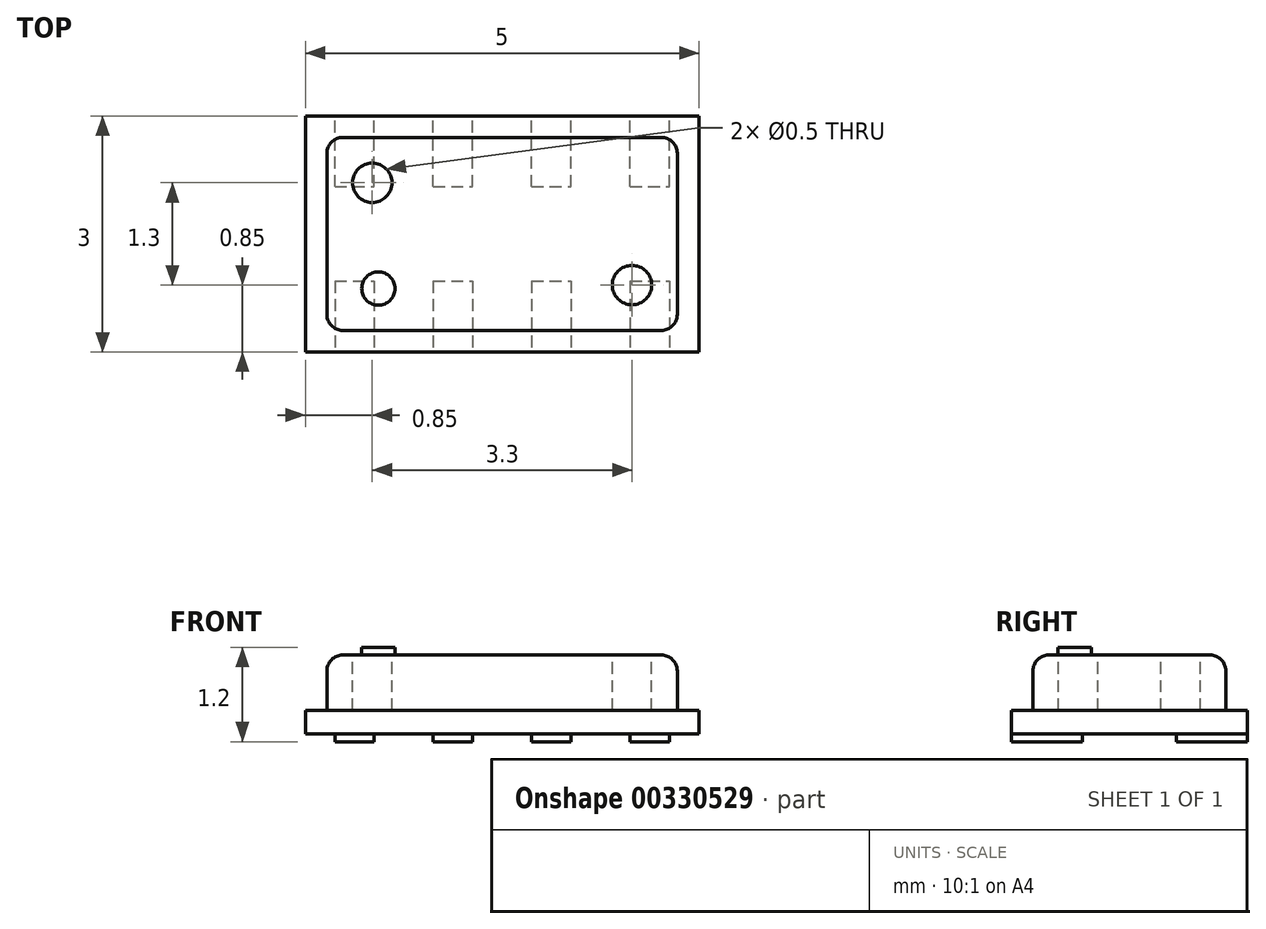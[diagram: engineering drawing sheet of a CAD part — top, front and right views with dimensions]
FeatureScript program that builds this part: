
annotation { "Feature Type Name" : "Feature", "Feature Type Description" : "" }
export const myFeature = defineFeature(function(context is Context, id is Id, definition is map)
    precondition{}
    {
        {
            var Q0;
            Q0=qCreatedBy(makeId("Top.planeOp"),FACE);
            var sketch = newSketch(context, id + "F0", { "sketchPlane" : qUnion([Q0])});
            skLineSegment(sketch, "E0.bottom", {"start": v(2.5, -1.5) * mm, "end": v(-2.5, -1.5) * mm});
            skLineSegment(sketch, "E0.top", {"start": v(2.5, 1.5) * mm, "end": v(-2.5, 1.5) * mm});
            skLineSegment(sketch, "E0.left", {"start": v(2.5, -1.5) * mm, "end": v(2.5, 1.5) * mm});
            skLineSegment(sketch, "E0.right", {"start": v(-2.5, -1.5) * mm, "end": v(-2.5, 1.5) * mm});
            skPoint(sketch, "E0.middle", {"position": v(0, 0) * mm});
            skSolve(sketch);
        }
        {
            var Q0;
            Q0 = qSketchRegion(id + "F0", true);
            extrude(context, id + "F1", {"entities" : qUnion([Q0]), "depth" : .3 * mm, "offsetDistance" : 25 * mm});
        }
        {
            var Q0;
            Q0=makeQuery(id+"F1.opExtrude","CAP_FACE",FACE,{"disambiguationData":[OSD([sQuery(id+"F0.wireOp",EDGE,"E0.bottom"),sQuery(id+"F0.wireOp",EDGE,"E0.top"),sQuery(id+"F0.wireOp",EDGE,"E0.left"),sQuery(id+"F0.wireOp",EDGE,"E0.right")])],"isStart":false});
            var sketch = newSketch(context, id + "F2", { "sketchPlane" : qUnion([Q0])});
            skLineSegment(sketch, "E1.bottom", {"start": v(2.23, -1.23) * mm, "end": v(-2.23, -1.23) * mm});
            skLineSegment(sketch, "E1.top", {"start": v(2.23, 1.23) * mm, "end": v(-2.23, 1.23) * mm});
            skLineSegment(sketch, "E1.left", {"start": v(2.23, -1.23) * mm, "end": v(2.23, 1.23) * mm});
            skLineSegment(sketch, "E1.right", {"start": v(-2.23, -1.23) * mm, "end": v(-2.23, 1.23) * mm});
            skPoint(sketch, "E1.middle", {"position": v(0, 0) * mm});
            skSolve(sketch);
        }
        {
            var Q0;
            Q0 = qSketchRegion(id + "F2", true);
            extrude(context, id + "F3", {"entities" : qUnion([Q0]), "depth" : .7 * mm, "offsetDistance" : 25 * mm});
        }
        {
            var Q0;
            Q0=makeQuery(id+"F3.opExtrude","CAP_EDGE",EDGE,{"disambiguationData":[OSD([sQuery(id+"F2.wireOp",EDGE,"E1.bottom")])],"isStart":false});
            var Q1;
            Q1=makeQuery(id+"F3.opExtrude","CAP_EDGE",EDGE,{"disambiguationData":[OSD([sQuery(id+"F2.wireOp",EDGE,"E1.left")])],"isStart":false});
            var Q2;
            Q2=makeQuery(id+"F3.opExtrude","CAP_EDGE",EDGE,{"disambiguationData":[OSD([sQuery(id+"F2.wireOp",EDGE,"E1.top")])],"isStart":false});
            var Q3;
            Q3=makeQuery(id+"F3.opExtrude","CAP_EDGE",EDGE,{"disambiguationData":[OSD([sQuery(id+"F2.wireOp",EDGE,"E1.right")])],"isStart":false});
            var Q4;
            Q4=makeQuery(id+"F3.opExtrude","SWEPT_EDGE",EDGE,{"disambiguationData":[OSD([sQuery(id+"F2.wireOp",EDGE,"E1.top"),sQuery(id+"F2.wireOp",EDGE,"E1.right")])]});
            var Q5;
            Q5=makeQuery(id+"F3.opExtrude","SWEPT_EDGE",EDGE,{"disambiguationData":[OSD([sQuery(id+"F2.wireOp",EDGE,"E1.bottom"),sQuery(id+"F2.wireOp",EDGE,"E1.right")])]});
            var Q6;
            Q6=makeQuery(id+"F3.opExtrude","SWEPT_EDGE",EDGE,{"disambiguationData":[OSD([sQuery(id+"F2.wireOp",EDGE,"E1.bottom"),sQuery(id+"F2.wireOp",EDGE,"E1.left")])]});
            var Q7;
            Q7=makeQuery(id+"F3.opExtrude","SWEPT_EDGE",EDGE,{"disambiguationData":[OSD([sQuery(id+"F2.wireOp",EDGE,"E1.top"),sQuery(id+"F2.wireOp",EDGE,"E1.left")])]});
            fillet(context, id + "F4", {"entities" : qUnion([Q0, Q1, Q2, Q3, Q4, Q5, Q6, Q7]), "radius" : .2 * mm, "tangentPropagation" : true, "allowEdgeOverflow" : false});
        }
        {
            var Q0;
            Q0=makeQuery(id+"F3.opExtrude","CAP_FACE",FACE,{"disambiguationData":[OSD([sQuery(id+"F2.wireOp",EDGE,"E1.bottom"),sQuery(id+"F2.wireOp",EDGE,"E1.top"),sQuery(id+"F2.wireOp",EDGE,"E1.left"),sQuery(id+"F2.wireOp",EDGE,"E1.right")])],"isStart":false});
            var sketch = newSketch(context, id + "F5", { "sketchPlane" : qUnion([Q0])});
            skCircle(sketch, "E2", {"center": v(1.65, -0.65) * mm, "radius": 0.25 * mm});
            skCircle(sketch, "E3", {"center": v(-1.65, 0.65) * mm, "radius": 0.25 * mm});
            skLineSegment(sketch, "E4", {"start": v(2.5, 0) * mm, "end": v(-2.43, 0) * mm, "construction": true});
            skLineSegment(sketch, "E5", {"start": v(0, 1.03) * mm, "end": v(0, -1.12) * mm, "construction": true});
            skPoint(sketch, "E5.endSnap0", {"position": v(0, -1.03) * mm});
            skSolve(sketch);
        }
        {
            var Q0;
            Q0 = qSketchRegion(id + "F5", true);
            extrude(context, id + "F6", {"entities" : qUnion([Q0]), "operationType" : NewBodyOperationType.REMOVE, "endBound" : BoundingType.UP_TO_NEXT, "oppositeDirection" : true, "depth" : 4 * mm, "offsetDistance" : 25 * mm});
        }
        {
            var Q0;
            Q0=makeQuery(id+"F1.opExtrude","CAP_FACE",FACE,{"disambiguationData":[OSD([sQuery(id+"F0.wireOp",EDGE,"E0.bottom"),sQuery(id+"F0.wireOp",EDGE,"E0.top"),sQuery(id+"F0.wireOp",EDGE,"E0.left"),sQuery(id+"F0.wireOp",EDGE,"E0.right")])],"isStart":true});
            var sketch = newSketch(context, id + "F7", { "sketchPlane" : qUnion([Q0])});
            skLineSegment(sketch, "E6", {"start": v(2.5, 0) * mm, "end": v(-2.5, 0) * mm, "construction": true});
            skLineSegment(sketch, "E7.bottom", {"start": v(1.63, 0.6) * mm, "end": v(2.12, 0.6) * mm});
            skLineSegment(sketch, "E7.top", {"start": v(1.63, 1.5) * mm, "end": v(2.12, 1.5) * mm});
            skLineSegment(sketch, "E7.left", {"start": v(1.63, 0.6) * mm, "end": v(1.63, 1.5) * mm});
            skLineSegment(sketch, "E7.right", {"start": v(2.12, 0.6) * mm, "end": v(2.12, 1.5) * mm});
            skPoint(sketch, "E7.middle", {"position": v(1.88, 1.05) * mm});
            skLineSegment(sketch, "E8", {"start": v(0, 1.5) * mm, "end": v(0, -0.09) * mm, "construction": true});
            skPoint(sketch, "E8.endSnap0", {"position": v(0, 1.5) * mm});
            skPoint(sketch, "E9.1.0.0", {"position": v(0.62, 1.05) * mm});
            skLineSegment(sketch, "E9.1.0.1", {"start": v(0.38, 0.6) * mm, "end": v(0.88, 0.6) * mm});
            skLineSegment(sketch, "E9.1.0.2", {"start": v(0.38, 1.5) * mm, "end": v(0.88, 1.5) * mm});
            skLineSegment(sketch, "E9.1.0.3", {"start": v(0.88, 0.6) * mm, "end": v(0.88, 1.5) * mm});
            skLineSegment(sketch, "E9.1.0.4", {"start": v(0.38, 0.6) * mm, "end": v(0.38, 1.5) * mm});
            skPoint(sketch, "E9.2.0.0", {"position": v(-0.63, 1.05) * mm});
            skLineSegment(sketch, "E9.2.0.1", {"start": v(-0.87, 0.6) * mm, "end": v(-0.37, 0.6) * mm});
            skLineSegment(sketch, "E9.2.0.2", {"start": v(-0.87, 1.5) * mm, "end": v(-0.37, 1.5) * mm});
            skLineSegment(sketch, "E9.2.0.3", {"start": v(-0.37, 0.6) * mm, "end": v(-0.37, 1.5) * mm});
            skLineSegment(sketch, "E9.2.0.4", {"start": v(-0.87, 0.6) * mm, "end": v(-0.87, 1.5) * mm});
            skPoint(sketch, "E9.3.0.0", {"position": v(-1.88, 1.05) * mm});
            skLineSegment(sketch, "E9.3.0.1", {"start": v(-2.12, 0.6) * mm, "end": v(-1.62, 0.6) * mm});
            skLineSegment(sketch, "E9.3.0.2", {"start": v(-2.12, 1.5) * mm, "end": v(-1.62, 1.5) * mm});
            skLineSegment(sketch, "E9.3.0.3", {"start": v(-1.62, 0.6) * mm, "end": v(-1.62, 1.5) * mm});
            skLineSegment(sketch, "E9.3.0.4", {"start": v(-2.12, 0.6) * mm, "end": v(-2.12, 1.5) * mm});
            skLineSegment(sketch, "E9.direction1", {"start": v(1.63, 0.6) * mm, "end": v(0.38, 0.6) * mm, "construction": true});
            skLineSegment(sketch, "E10.MirrorCS", {"start": v(0.38, -0.6) * mm, "end": v(0.88, -0.6) * mm});
            skLineSegment(sketch, "E11.MirrorCS", {"start": v(0.37, -1.5) * mm, "end": v(0.87, -1.5) * mm});
            skLineSegment(sketch, "E12.MirrorCS", {"start": v(2.12, -0.6) * mm, "end": v(2.12, -1.5) * mm});
            skLineSegment(sketch, "E13.MirrorCS", {"start": v(1.62, -0.6) * mm, "end": v(1.62, -1.5) * mm});
            skLineSegment(sketch, "E14.MirrorCS", {"start": v(1.62, -1.5) * mm, "end": v(2.12, -1.5) * mm});
            skLineSegment(sketch, "E15.MirrorCS", {"start": v(1.62, -0.6) * mm, "end": v(2.12, -0.6) * mm});
            skLineSegment(sketch, "E16.MirrorCS", {"start": v(-2.12, -1.5) * mm, "end": v(-1.63, -1.5) * mm});
            skPoint(sketch, "E17.MirrorP", {"position": v(1.87, -1.05) * mm});
            skLineSegment(sketch, "E18.MirrorCS", {"start": v(-2.12, -0.6) * mm, "end": v(-1.62, -0.6) * mm});
            skLineSegment(sketch, "E19.MirrorCS", {"start": v(-0.88, -0.6) * mm, "end": v(-0.88, -1.5) * mm});
            skPoint(sketch, "E20.MirrorP", {"position": v(-1.88, -1.05) * mm});
            skLineSegment(sketch, "E21.MirrorCS", {"start": v(-2.12, -0.6) * mm, "end": v(-2.12, -1.5) * mm});
            skPoint(sketch, "E22.MirrorP", {"position": v(0.62, -1.05) * mm});
            skLineSegment(sketch, "E23.MirrorCS", {"start": v(1.62, -0.6) * mm, "end": v(0.37, -0.6) * mm, "construction": true});
            skLineSegment(sketch, "E24.MirrorCS", {"start": v(0.88, -0.6) * mm, "end": v(0.87, -1.5) * mm});
            skPoint(sketch, "E25.MirrorP", {"position": v(0, -1.5) * mm});
            skLineSegment(sketch, "E26.MirrorCS", {"start": v(-1.62, -0.6) * mm, "end": v(-1.62, -1.5) * mm});
            skLineSegment(sketch, "E27.MirrorCS", {"start": v(-0.88, -0.6) * mm, "end": v(-0.38, -0.6) * mm});
            skPoint(sketch, "E28.MirrorP", {"position": v(-0.63, -1.05) * mm});
            skLineSegment(sketch, "E29.MirrorCS", {"start": v(-0.88, -1.5) * mm, "end": v(-0.38, -1.5) * mm});
            skLineSegment(sketch, "E30.MirrorCS", {"start": v(-0.38, -0.6) * mm, "end": v(-0.38, -1.5) * mm});
            skLineSegment(sketch, "E31.MirrorCS", {"start": v(0.37, -0.6) * mm, "end": v(0.37, -1.5) * mm});
            skSolve(sketch);
        }
        {
            var Q0;
            Q0 = qSketchRegion(id + "F7", true);
            extrude(context, id + "F8", {"entities" : qUnion([Q0]), "depth" : .1 * mm, "offsetDistance" : 25 * mm});
        }
        {
            var Q0;
            Q0=makeQuery(id+"F3.opExtrude","CAP_FACE",FACE,{"disambiguationData":[OSD([sQuery(id+"F2.wireOp",EDGE,"E1.bottom"),sQuery(id+"F2.wireOp",EDGE,"E1.top"),sQuery(id+"F2.wireOp",EDGE,"E1.left"),sQuery(id+"F2.wireOp",EDGE,"E1.right")])],"isStart":false});
            var sketch = newSketch(context, id + "F9", { "sketchPlane" : qUnion([Q0])});
            skCircle(sketch, "E32", {"center": v(-1.57, -0.7) * mm, "radius": 0.21 * mm});
            skSolve(sketch);
        }
        {
            var Q0;
            Q0 = qSketchRegion(id + "F9", true);
            extrude(context, id + "F10", {"entities" : qUnion([Q0]), "depth" : .1 * mm, "offsetDistance" : 25 * mm});
        }
    });
